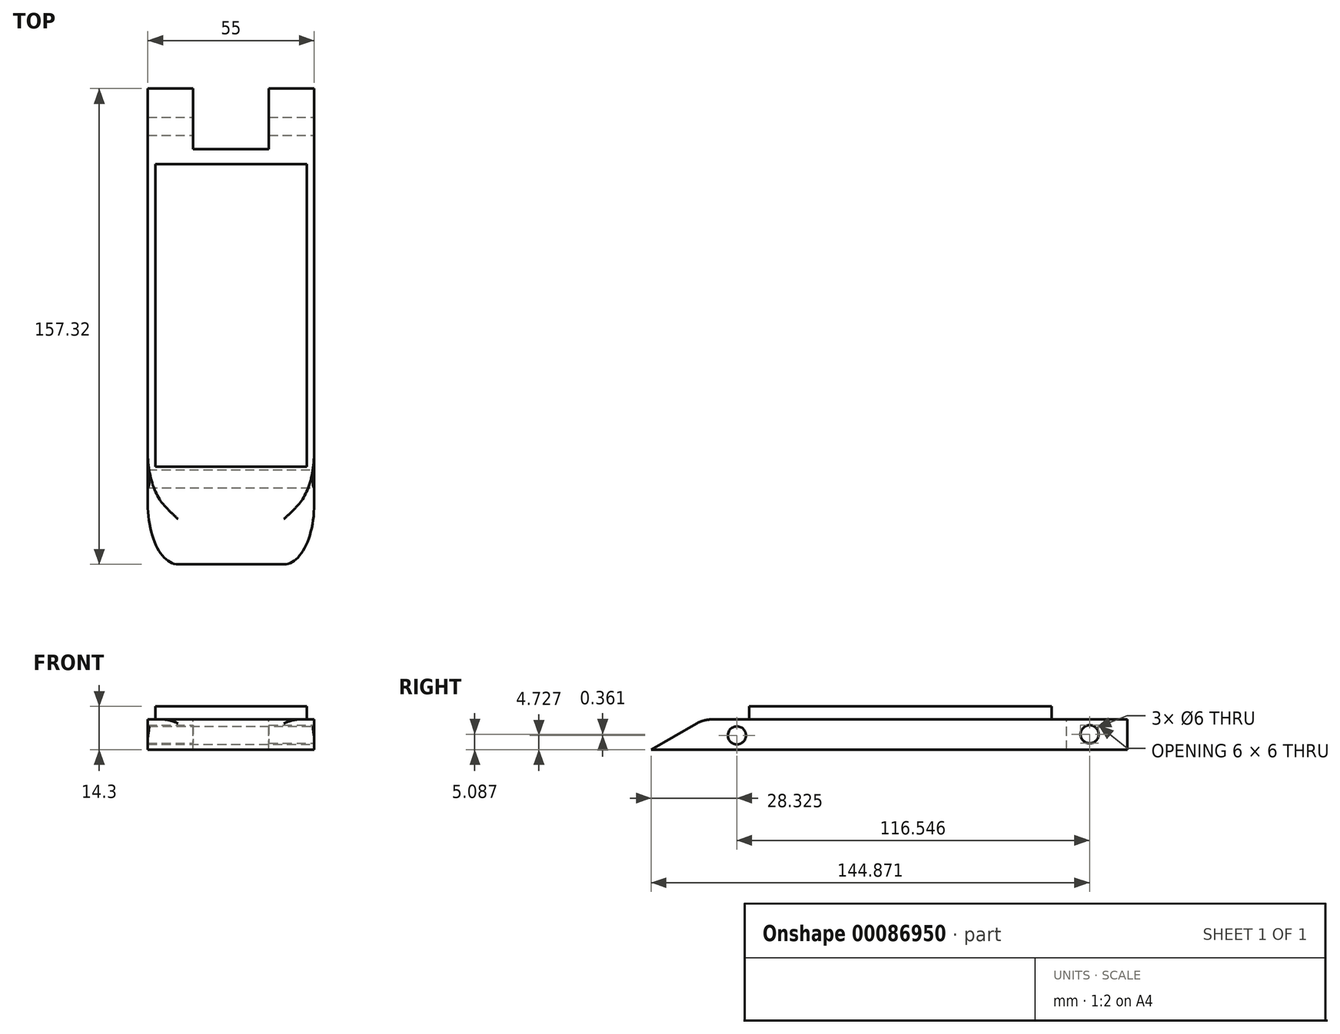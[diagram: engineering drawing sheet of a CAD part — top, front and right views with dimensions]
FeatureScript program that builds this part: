
annotation { "Feature Type Name" : "Feature", "Feature Type Description" : "" }
export const myFeature = defineFeature(function(context is Context, id is Id, definition is map)
    precondition{}
    {
        {
            var Q0;
            Q0=qCreatedBy(makeId("Right.planeOp"),FACE);
            var sketch = newSketch(context, id + "F0", { "sketchPlane" : qUnion([Q0])});
            skLineSegment(sketch, "E0.bottom", {"start": v(-80, -0.6) * mm, "end": v(100, -0.6) * mm});
            skLineSegment(sketch, "E0.top", {"start": v(-80, -10.6) * mm, "end": v(100, -10.6) * mm});
            skLineSegment(sketch, "E0.left", {"start": v(-80, -0.6) * mm, "end": v(-80, -10.6) * mm});
            skLineSegment(sketch, "E0.right", {"start": v(100, -0.6) * mm, "end": v(100, -10.6) * mm});
            skSolve(sketch);
        }
        {
            var Q0;
            Q0=makeQuery(id+"F0.imprint","IMPRINT",FACE,{"disambiguationData":[TD([[makeQuery(id+"F0.imprint","IMPRINT",EDGE,{"derivedFrom":sQuery(id+"F0.wireOp",EDGE,"E0.bottom")}),-1.0]])]});
            extrude(context, id + "F1", {"entities" : qUnion([Q0]), "endBound" : BoundingType.SYMMETRIC, "oppositeDirection" : true, "depth" : 55 * mm});
        }
        {
            var Q0;
            Q0=makeQuery(id+"F1.opExtrude","SWEPT_EDGE",EDGE,{"disambiguationData":[OSD([sQuery(id+"F0.wireOp",EDGE,"E0.bottom"),sQuery(id+"F0.wireOp",EDGE,"E0.left")])]});
            chamfer(context, id + "F2", {"entities" : qUnion([Q0]), "chamferType" : ChamferType.OFFSET_ANGLE, "width" : 40 * mm, "oppositeDirection" : false, "angle" : 30 * degree, "tangentPropagation" : true});
        }
        {
            var Q0;
            {var subQ0=sQuery(id+"F0.wireOp",EDGE,"E0.left");var subQ1=sQuery(id+"F0.wireOp",EDGE,"E0.bottom");Q0=makeQuery(id+"F2.opChamfer","BLEND_EDGE",EDGE,{"blendedFrom":[makeQuery(id+"F1.opExtrude","SWEPT_EDGE",EDGE,{"disambiguationData":[OSD([subQ1,subQ0])]}),makeQuery(id+"F1.opExtrude","CAP_FACE",FACE,{"disambiguationData":[OSD([subQ1,sQuery(id+"F0.wireOp",EDGE,"E0.top"),subQ0,sQuery(id+"F0.wireOp",EDGE,"E0.right")])],"isStart":false})],"blendedInto":[makeQuery(id+"F1.opExtrude","CAP_FACE",FACE,{"disambiguationData":[OSD([subQ1,sQuery(id+"F0.wireOp",EDGE,"E0.top"),subQ0,sQuery(id+"F0.wireOp",EDGE,"E0.right")])],"isStart":false})]});}
            var Q1;
            {var subQ0=sQuery(id+"F0.wireOp",EDGE,"E0.left");var subQ1=sQuery(id+"F0.wireOp",EDGE,"E0.bottom");Q1=makeQuery(id+"F2.opChamfer","BLEND_EDGE",EDGE,{"blendedFrom":[makeQuery(id+"F1.opExtrude","SWEPT_EDGE",EDGE,{"disambiguationData":[OSD([subQ1,subQ0])]}),makeQuery(id+"F1.opExtrude","CAP_FACE",FACE,{"disambiguationData":[OSD([subQ1,sQuery(id+"F0.wireOp",EDGE,"E0.top"),subQ0,sQuery(id+"F0.wireOp",EDGE,"E0.right")])],"isStart":true})],"blendedInto":[makeQuery(id+"F1.opExtrude","CAP_FACE",FACE,{"disambiguationData":[OSD([subQ1,sQuery(id+"F0.wireOp",EDGE,"E0.top"),subQ0,sQuery(id+"F0.wireOp",EDGE,"E0.right")])],"isStart":true})]});}
            var Q2;
            {var subQ0=sQuery(id+"F0.wireOp",EDGE,"E0.bottom");Q2=makeQuery(id+"F2.opChamfer","BLEND_EDGE",EDGE,{"blendedFrom":[makeQuery(id+"F1.opExtrude","SWEPT_EDGE",EDGE,{"disambiguationData":[OSD([subQ0,sQuery(id+"F0.wireOp",EDGE,"E0.left")])]}),makeQuery(id+"F1.opExtrude","SWEPT_FACE",FACE,{"disambiguationData":[OSD([subQ0])]})],"blendedInto":[makeQuery(id+"F1.opExtrude","SWEPT_FACE",FACE,{"disambiguationData":[OSD([subQ0])]})]});}
            fillet(context, id + "F3", {"entities" : qUnion([Q0, Q1, Q2]), "radius" : 10 * mm, "tangentPropagation" : true, "allowEdgeOverflow" : false});
        }
        {
            var Q0;
            Q0=makeQuery(id+"F1.opExtrude","SWEPT_FACE",FACE,{"disambiguationData":[OSD([sQuery(id+"F0.wireOp",EDGE,"E0.bottom")])]});
            var Q1;
            Q1=makeQuery(id+"F1.opExtrude","SWEPT_FACE",FACE,{"disambiguationData":[OSD([sQuery(id+"F0.wireOp",EDGE,"E0.bottom")])]});
            var sketch = newSketch(context, id + "F4", { "sketchPlane" : qUnion([Q0, Q1])});
            skLineSegment(sketch, "E1.bottom", {"start": v(-25, 75) * mm, "end": v(25, 75) * mm});
            skLineSegment(sketch, "E1.top", {"start": v(-25, -25) * mm, "end": v(25, -25) * mm});
            skLineSegment(sketch, "E1.left", {"start": v(-25, 75) * mm, "end": v(-25, -25) * mm});
            skLineSegment(sketch, "E1.right", {"start": v(25, 75) * mm, "end": v(25, -25) * mm});
            skSolve(sketch);
        }
        {
            var Q0;
            Q0=makeQuery(id+"F4.imprint","IMPRINT",FACE,{"disambiguationData":[TD([[makeQuery(id+"F4.imprint","IMPRINT",EDGE,{"derivedFrom":sQuery(id+"F4.wireOp",EDGE,"E1.bottom")}),-1.0]])]});
            extrude(context, id + "F5", {"entities" : qUnion([Q0]), "operationType" : NewBodyOperationType.ADD, "depth" : 4.3 * mm});
        }
        {
            var Q0;
            Q0=makeQuery(id+"F1.opExtrude","SWEPT_FACE",FACE,{"disambiguationData":[OSD([sQuery(id+"F0.wireOp",EDGE,"E0.bottom")])]});
            var Q1;
            Q1=makeQuery(id+"F1.opExtrude","SWEPT_FACE",FACE,{"disambiguationData":[OSD([sQuery(id+"F0.wireOp",EDGE,"E0.bottom")])]});
            var sketch = newSketch(context, id + "F6", { "sketchPlane" : qUnion([Q0, Q1])});
            skLineSegment(sketch, "E2.bottom", {"start": v(-12.5, 100) * mm, "end": v(12.5, 100) * mm});
            skLineSegment(sketch, "E2.top", {"start": v(-12.5, 80) * mm, "end": v(12.5, 80) * mm});
            skLineSegment(sketch, "E2.left", {"start": v(-12.5, 100) * mm, "end": v(-12.5, 80) * mm});
            skLineSegment(sketch, "E2.right", {"start": v(12.5, 100) * mm, "end": v(12.5, 80) * mm});
            skSolve(sketch);
        }
        {
            var Q0;
            Q0=makeQuery(id+"F6.imprint","IMPRINT",FACE,{"disambiguationData":[TD([[makeQuery(id+"F6.imprint","IMPRINT",EDGE,{"derivedFrom":sQuery(id+"F6.wireOp",EDGE,"E2.bottom")}),-1.0]])]});
            extrude(context, id + "F7", {"entities" : qUnion([Q0]), "operationType" : NewBodyOperationType.REMOVE, "oppositeDirection" : true, "depth" : 25 * mm});
        }
        {
            var Q0;
            Q0=makeQuery(id+"F1.opExtrude","CAP_FACE",FACE,{"disambiguationData":[OSD([sQuery(id+"F0.wireOp",EDGE,"E0.bottom"),sQuery(id+"F0.wireOp",EDGE,"E0.top"),sQuery(id+"F0.wireOp",EDGE,"E0.left"),sQuery(id+"F0.wireOp",EDGE,"E0.right")])],"isStart":true});
            var sketch = newSketch(context, id + "F8", { "sketchPlane" : qUnion([Q0])});
            skCircle(sketch, "E3", {"center": v(-29, -5.86) * mm, "radius": 3 * mm});
            skCircle(sketch, "E4", {"center": v(87.55, -5.5) * mm, "radius": 3 * mm});
            skSolve(sketch);
        }
        {
            var Q0;
            Q0=sQuery(id+"F8.wireOp",VERTEX,"E3.center");
            var Q1;
            Q1=makeQuery(id+"F1.opExtrude","SWEPT_BODY",BODY,{"disambiguationData":[OSD([sQuery(id+"F0.wireOp",EDGE,"E0.bottom"),sQuery(id+"F0.wireOp",EDGE,"E0.top"),sQuery(id+"F0.wireOp",EDGE,"E0.left"),sQuery(id+"F0.wireOp",EDGE,"E0.right")])]});
            hole(context, id + "F9", {"style" : HoleStyle.SIMPLE, "endStyle" : HoleEndStyle.THROUGH, "holeDiameter" : 6 * mm, "startFromSketch" : true, "locations" : qUnion([Q0]), "scope" : qUnion([Q1]), "isTappedThrough" : true});
        }
        {
            var Q0;
            Q0=sQuery(id+"F8.wireOp",VERTEX,"E4.center");
            var Q1;
            Q1=makeQuery(id+"F1.opExtrude","SWEPT_BODY",BODY,{"disambiguationData":[OSD([sQuery(id+"F0.wireOp",EDGE,"E0.bottom"),sQuery(id+"F0.wireOp",EDGE,"E0.top"),sQuery(id+"F0.wireOp",EDGE,"E0.left"),sQuery(id+"F0.wireOp",EDGE,"E0.right")])]});
            hole(context, id + "F10", {"style" : HoleStyle.SIMPLE, "endStyle" : HoleEndStyle.THROUGH, "holeDiameter" : 6 * mm, "startFromSketch" : true, "locations" : qUnion([Q0]), "scope" : qUnion([Q1]), "isTappedThrough" : true});
        }
    });
